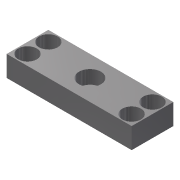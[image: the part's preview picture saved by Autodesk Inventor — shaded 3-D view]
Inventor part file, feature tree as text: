
AUTODESK INVENTOR PART (.ipt)
format: ipt  version: 2015 (Build 190159000, 159)  size: 136,704 bytes
history: native  units: mm
features: hole x5, extrude x1, sketch x1
ambient origin geometry x8: Origin, YZ Plane, XZ Plane, XY Plane, X Axis, Y Axis, Z Axis, Center Point
bodies: Body1 (feature_tree)
feature tree (7):
  extrude  "Extrusion2"  Depth=20.0mm
  hole  "Hole2"  [1 undecoded]
  hole  "Hole3"  [1 undecoded]
  hole  "Hole4"  [1 undecoded]
  hole  "Hole5"  [1 undecoded]
  hole  "Hole6"  [1 undecoded]
  sketch  "Sketch4"  dims[d37=60.0mm d38=20.0mm d39=10.0mm d40=0.0mm d41=10.0mm d42=30.0mm d43=6.5mm d44=6.0mm d45=10.5mm d46=6.5mm d47=90.0deg d48=10.0mm d49=20.594885mm d50=5.0mm d51=5.0mm d52=5.5mm d53=6.0mm d54=9.0mm d55=8.0mm d56=90.0deg d57=10.0mm d58=20.594885mm d59=5.0mm d60=5.0mm d61=5.5mm d62=6.0mm d63=9.0mm d64=8.0mm d65=90.0deg d66=10.0mm d67=20.594885mm d68=5.0mm d69=5.0mm d70=5.5mm d71=6.0mm d72=9.0mm d73=8.0mm d74=90.0deg d75=10.0mm d76=20.594885mm d77=5.0mm d78=5.0mm d79=5.5mm d80=6.0mm d81=9.0mm d82=8.0mm d83=90.0deg d84=10.0mm d85=20.594885mm]
note: 5 required parameter values undecoded (feature->parameter linkage not recoverable at this tier; creation-order binding heuristic only, values carry confidence <= 0.55)
